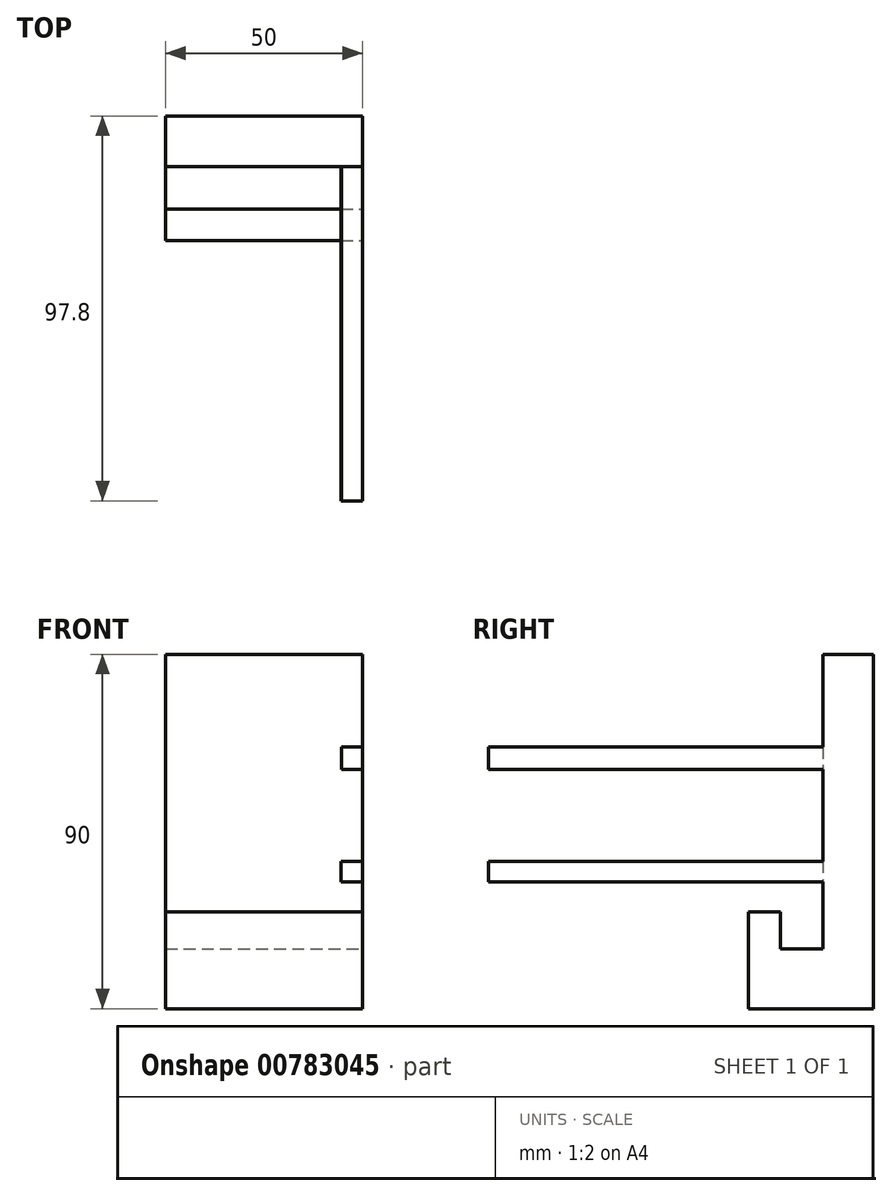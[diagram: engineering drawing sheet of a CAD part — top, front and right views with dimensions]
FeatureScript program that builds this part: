
annotation { "Feature Type Name" : "Feature", "Feature Type Description" : "" }
export const myFeature = defineFeature(function(context is Context, id is Id, definition is map)
    precondition{}
    {
        {
            var Q0;
            Q0=qCreatedBy(makeId("Right.planeOp"),FACE);
            var sketch = newSketch(context, id + "F0", { "sketchPlane" : qUnion([Q0])});
            skLineSegment(sketch, "E0", {"start": v(5.03, 57.73) * mm, "end": v(-7.77, 57.73) * mm});
            skLineSegment(sketch, "E1", {"start": v(-7.77, 57.73) * mm, "end": v(-7.77, -17.1) * mm});
            skLineSegment(sketch, "E2", {"start": v(-7.77, -17.1) * mm, "end": v(-18.56, -17.1) * mm});
            skLineSegment(sketch, "E3", {"start": v(-18.56, -17.1) * mm, "end": v(-18.56, -7.66) * mm});
            skLineSegment(sketch, "E4", {"start": v(-18.56, -7.66) * mm, "end": v(-26.65, -7.66) * mm});
            skLineSegment(sketch, "E5", {"start": v(-26.65, -7.66) * mm, "end": v(-26.65, -32.27) * mm});
            skLineSegment(sketch, "E6", {"start": v(-26.65, -32.27) * mm, "end": v(5.03, -32.27) * mm});
            skLineSegment(sketch, "E7", {"start": v(5.03, -32.27) * mm, "end": v(5.03, 57.73) * mm});
            skSolve(sketch);
        }
        {
            var Q0;
            Q0=makeQuery(id+"F0.imprint","IMPRINT",FACE,{"disambiguationData":[TD([[makeQuery(id+"F0.imprint","IMPRINT",EDGE,{"derivedFrom":sQuery(id+"F0.wireOp",EDGE,"E0")}),1.0]])]});
            extrude(context, id + "F1", {"entities" : qUnion([Q0]), "oppositeDirection" : true, "depth" : 50 * mm, "offsetDistance" : 25 * mm});
        }
        {
            var Q0;
            Q0=makeQuery(id+"F1.opExtrude","SWEPT_FACE",FACE,{"disambiguationData":[OSD([sQuery(id+"F0.wireOp",EDGE,"E1")])]});
            var sketch = newSketch(context, id + "F2", { "sketchPlane" : qUnion([Q0])});
            skLineSegment(sketch, "E8", {"start": v(0, 57.73) * mm, "end": v(0, 34.22) * mm});
            skLineSegment(sketch, "E9", {"start": v(0, 34.22) * mm, "end": v(0, 5.17) * mm});
            skLineSegment(sketch, "E10", {"start": v(0, 5.17) * mm, "end": v(0, -17.1) * mm});
            skLineSegment(sketch, "E11.bottom", {"start": v(0, 34.22) * mm, "end": v(-5.34, 34.22) * mm});
            skLineSegment(sketch, "E11.top", {"start": v(0, 28.57) * mm, "end": v(-5.34, 28.57) * mm});
            skLineSegment(sketch, "E11.left", {"start": v(0, 34.22) * mm, "end": v(0, 28.57) * mm});
            skLineSegment(sketch, "E11.right", {"start": v(-5.34, 34.22) * mm, "end": v(-5.34, 28.57) * mm});
            skLineSegment(sketch, "E12.bottom", {"start": v(0, 5.17) * mm, "end": v(-5.4, 5.17) * mm});
            skLineSegment(sketch, "E12.top", {"start": v(0, 0) * mm, "end": v(-5.4, 0) * mm});
            skLineSegment(sketch, "E12.left", {"start": v(0, 5.17) * mm, "end": v(0, 0) * mm});
            skLineSegment(sketch, "E12.right", {"start": v(-5.4, 5.17) * mm, "end": v(-5.4, 0) * mm});
            skSolve(sketch);
        }
        {
            var Q0;
            Q0=makeQuery(id+"F2.imprint","IMPRINT",FACE,{"disambiguationData":[TD([[makeQuery(id+"F2.imprint","IMPRINT",EDGE,{"derivedFrom":sQuery(id+"F2.wireOp",EDGE,"E11.bottom")}),1.0]])]});
            var Q1;
            Q1=makeQuery(id+"F2.imprint","IMPRINT",FACE,{"disambiguationData":[TD([[makeQuery(id+"F2.imprint","IMPRINT",EDGE,{"derivedFrom":sQuery(id+"F2.wireOp",EDGE,"E12.bottom")}),1.0]])]});
            extrude(context, id + "F3", {"entities" : qUnion([Q0, Q1]), "operationType" : NewBodyOperationType.ADD, "depth" : 85 * mm, "offsetDistance" : 25 * mm});
        }
    });
